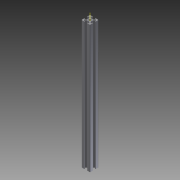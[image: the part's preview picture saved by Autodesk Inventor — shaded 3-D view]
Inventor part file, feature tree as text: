
AUTODESK INVENTOR PART (.ipt)
format: ipt  version: 2012 (Build 160160000, 160)  size: 207,360 bytes
history: native  units: mm
features: extrude x1, other x1, pattern_circular x1, sketch x1
ambient origin geometry x8: Origin, YZ Plane, XZ Plane, XY Plane, X Axis, Y Axis, Z Axis, Center Point
feature tree (4):
  extrude  "Extrusion2"  Depth=10.0mm
  other  "Work Axis5"
  pattern_circular  "Circular Pattern2"  [2 undecoded]
  sketch  "Sketch1"  dims[d0=10.0mm d1=10.0mm d3=1.4mm d4=6.1mm d5=6.1mm d6=3.1mm d7=3.1mm d8=2.5mm d9=5.7mm d10=5.7mm d12=2.0mm d14=2.5mm d15=3.2mm d21=1.2mm d22=0.5mm d23=0.5mm d24=0.5mm d25=0.5mm d26=0.2mm d27=0.2mm d28=0.2mm d29=0.2mm d30=300.0mm d31=0.0mm d32=40.0mm d33=360.0deg d48=0.1mm d67=4.0mm]
note: 2 required parameter values undecoded (feature->parameter linkage not recoverable at this tier; creation-order binding heuristic only, values carry confidence <= 0.55)
